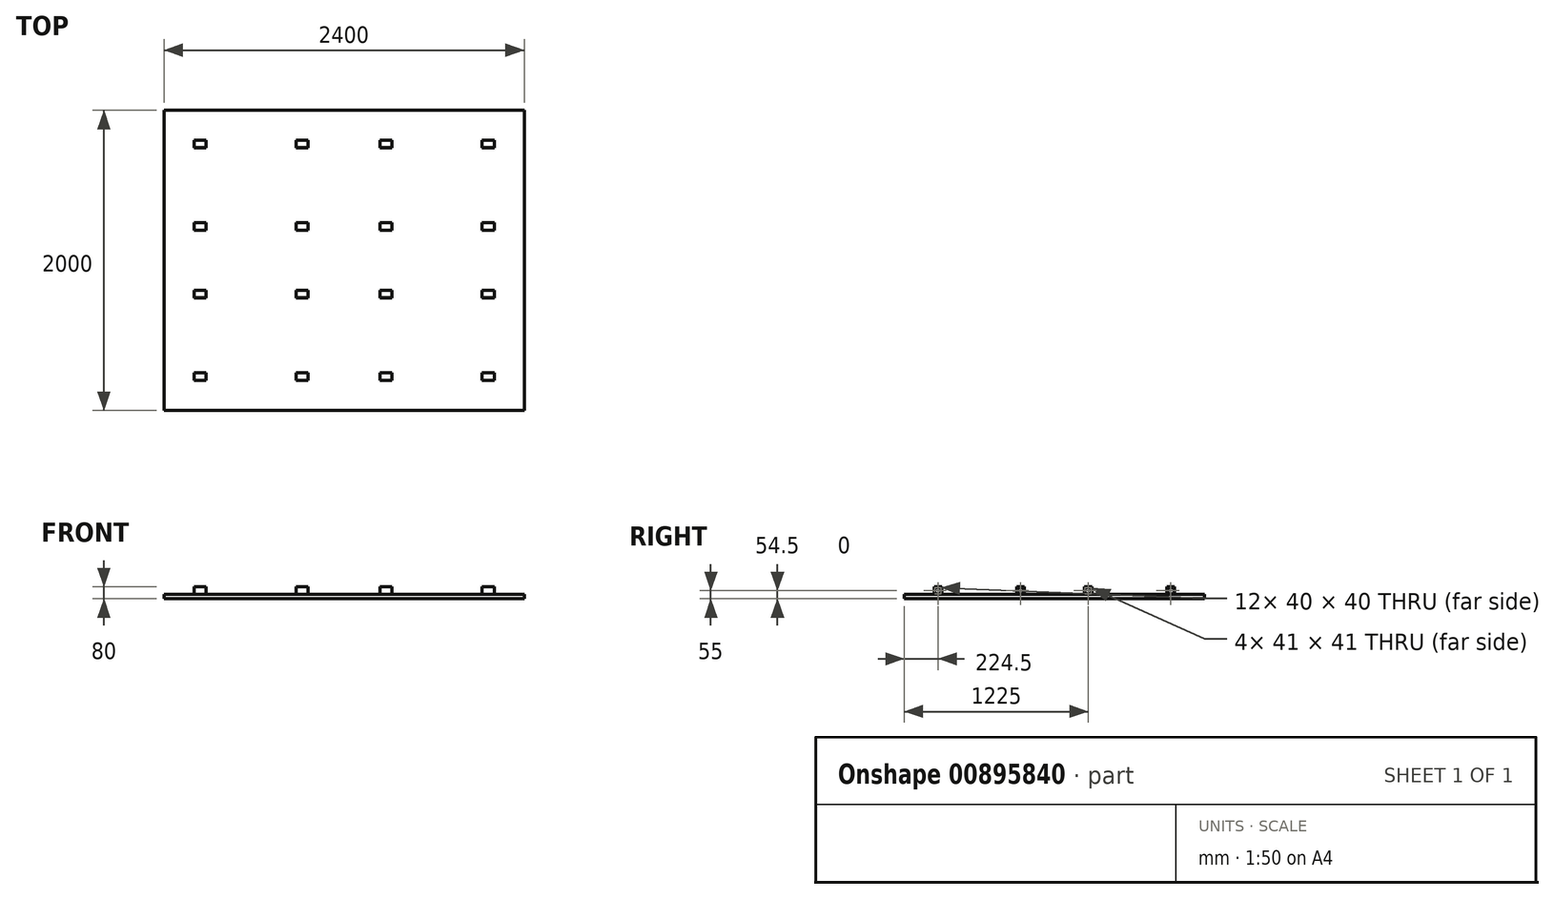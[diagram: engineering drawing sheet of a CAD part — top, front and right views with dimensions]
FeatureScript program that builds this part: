
annotation { "Feature Type Name" : "Feature", "Feature Type Description" : "" }
export const myFeature = defineFeature(function(context is Context, id is Id, definition is map)
    precondition{}
    {
        {
            var Q0;
            Q0=qCreatedBy(makeId("Top.planeOp"),FACE);
            var sketch = newSketch(context, id + "F0", { "sketchPlane" : qUnion([Q0])});
            skLineSegment(sketch, "E0.bottom", {"start": v(0, 0) * mm, "end": v(1200, 0) * mm});
            skLineSegment(sketch, "E0.top", {"start": v(0, 1000) * mm, "end": v(1200, 1000) * mm});
            skLineSegment(sketch, "E0.left", {"start": v(0, 0) * mm, "end": v(0, 1000) * mm});
            skLineSegment(sketch, "E0.right", {"start": v(1200, 0) * mm, "end": v(1200, 1000) * mm});
            skLineSegment(sketch, "E1.MirrorCS", {"start": v(1200, 0) * mm, "end": v(1200, -1000) * mm});
            skLineSegment(sketch, "E2.MirrorCS", {"start": v(0, -1000) * mm, "end": v(1200, -1000) * mm});
            skLineSegment(sketch, "E3.MirrorCS", {"start": v(0, 0) * mm, "end": v(0, -1000) * mm});
            skLineSegment(sketch, "E4.MirrorCS", {"start": v(0, 1000) * mm, "end": v(-1200, 1000) * mm});
            skLineSegment(sketch, "E5.MirrorCS", {"start": v(0, 0) * mm, "end": v(-1200, 0) * mm});
            skLineSegment(sketch, "E6.MirrorCS", {"start": v(-1200, 0) * mm, "end": v(-1200, 1000) * mm});
            skLineSegment(sketch, "E7.MirrorCS", {"start": v(0, -1000) * mm, "end": v(-1200, -1000) * mm});
            skLineSegment(sketch, "E8.MirrorCS", {"start": v(-1200, 0) * mm, "end": v(-1200, -1000) * mm});
            skSolve(sketch);
        }
        {
            var Q0;
            Q0=makeQuery(id+"F0.imprint","IMPRINT",FACE,{"disambiguationData":[TD([[makeQuery(id+"F0.imprint","IMPRINT",EDGE,{"derivedFrom":sQuery(id+"F0.wireOp",EDGE,"E4.MirrorCS")}),1.0]])]});
            var Q1;
            Q1=makeQuery(id+"F0.imprint","IMPRINT",FACE,{"disambiguationData":[TD([[makeQuery(id+"F0.imprint","IMPRINT",EDGE,{"derivedFrom":sQuery(id+"F0.wireOp",EDGE,"E0.top")}),-1.0]])]});
            var Q2;
            Q2=makeQuery(id+"F0.imprint","IMPRINT",FACE,{"disambiguationData":[TD([[makeQuery(id+"F0.imprint","IMPRINT",EDGE,{"derivedFrom":sQuery(id+"F0.wireOp",EDGE,"E1.MirrorCS")}),-1.0]])]});
            var Q3;
            Q3=makeQuery(id+"F0.imprint","IMPRINT",FACE,{"disambiguationData":[TD([[makeQuery(id+"F0.imprint","IMPRINT",EDGE,{"derivedFrom":sQuery(id+"F0.wireOp",EDGE,"E5.MirrorCS")}),1.0]])]});
            extrude(context, id + "F1", {"entities" : qUnion([Q0, Q1, Q2, Q3]), "depth" : 30 * mm, "offsetDistance" : 25 * mm});
        }
        {
            var Q0;
            Q0=makeQuery(id+"F1.opExtrude","CAP_FACE",FACE,{"disambiguationData":[OSD([sQuery(id+"F0.wireOp",EDGE,"E0.top"),sQuery(id+"F0.wireOp",EDGE,"E0.right"),sQuery(id+"F0.wireOp",EDGE,"E1.MirrorCS"),sQuery(id+"F0.wireOp",EDGE,"E2.MirrorCS"),sQuery(id+"F0.wireOp",EDGE,"E4.MirrorCS"),sQuery(id+"F0.wireOp",EDGE,"E6.MirrorCS"),sQuery(id+"F0.wireOp",EDGE,"E7.MirrorCS"),sQuery(id+"F0.wireOp",EDGE,"E8.MirrorCS")])],"isStart":false});
            var sketch = newSketch(context, id + "F2", { "sketchPlane" : qUnion([Q0])});
            skLineSegment(sketch, "E9.bottom", {"start": v(-1000, 800) * mm, "end": v(-920, 800) * mm});
            skLineSegment(sketch, "E9.top", {"start": v(-1000, 750) * mm, "end": v(-920, 750) * mm});
            skLineSegment(sketch, "E9.left", {"start": v(-1000, 800) * mm, "end": v(-1000, 750) * mm});
            skLineSegment(sketch, "E9.right", {"start": v(-920, 800) * mm, "end": v(-920, 750) * mm});
            skLineSegment(sketch, "E10.bottom", {"start": v(-320, 800) * mm, "end": v(-240, 800) * mm});
            skLineSegment(sketch, "E10.top", {"start": v(-320, 750) * mm, "end": v(-240, 750) * mm});
            skLineSegment(sketch, "E10.left", {"start": v(-320, 800) * mm, "end": v(-320, 750) * mm});
            skLineSegment(sketch, "E10.right", {"start": v(-240, 800) * mm, "end": v(-240, 750) * mm});
            skLineSegment(sketch, "E11.bottom", {"start": v(240, 800) * mm, "end": v(320, 800) * mm});
            skLineSegment(sketch, "E11.top", {"start": v(240, 750) * mm, "end": v(320, 750) * mm});
            skLineSegment(sketch, "E11.left", {"start": v(240, 800) * mm, "end": v(240, 750) * mm});
            skLineSegment(sketch, "E11.right", {"start": v(320, 800) * mm, "end": v(320, 750) * mm});
            skLineSegment(sketch, "E12.bottom", {"start": v(920, 800) * mm, "end": v(1000, 800) * mm});
            skLineSegment(sketch, "E12.top", {"start": v(920, 750) * mm, "end": v(1000, 750) * mm});
            skLineSegment(sketch, "E12.left", {"start": v(920, 800) * mm, "end": v(920, 750) * mm});
            skLineSegment(sketch, "E12.right", {"start": v(1000, 800) * mm, "end": v(1000, 750) * mm});
            skLineSegment(sketch, "E13.MirrorCS", {"start": v(-1000, -800) * mm, "end": v(-1000, -750) * mm});
            skLineSegment(sketch, "E14.MirrorCS", {"start": v(-1000, -800) * mm, "end": v(-920, -800) * mm});
            skLineSegment(sketch, "E15.MirrorCS", {"start": v(-920, -800) * mm, "end": v(-920, -750) * mm});
            skLineSegment(sketch, "E16.MirrorCS", {"start": v(-1000, -750) * mm, "end": v(-920, -750) * mm});
            skLineSegment(sketch, "E17.MirrorCS", {"start": v(-320, -800) * mm, "end": v(-240, -800) * mm});
            skLineSegment(sketch, "E18.MirrorCS", {"start": v(-240, -800) * mm, "end": v(-240, -750) * mm});
            skLineSegment(sketch, "E19.MirrorCS", {"start": v(-320, -750) * mm, "end": v(-240, -750) * mm});
            skLineSegment(sketch, "E20.MirrorCS", {"start": v(-320, -800) * mm, "end": v(-320, -750) * mm});
            skLineSegment(sketch, "E21.MirrorCS", {"start": v(240, -800) * mm, "end": v(320, -800) * mm});
            skLineSegment(sketch, "E22.MirrorCS", {"start": v(240, -800) * mm, "end": v(240, -750) * mm});
            skLineSegment(sketch, "E23.MirrorCS", {"start": v(240, -750) * mm, "end": v(320, -750) * mm});
            skLineSegment(sketch, "E24.MirrorCS", {"start": v(320, -800) * mm, "end": v(320, -750) * mm});
            skLineSegment(sketch, "E25.MirrorCS", {"start": v(920, -800) * mm, "end": v(1000, -800) * mm});
            skLineSegment(sketch, "E26.MirrorCS", {"start": v(920, -800) * mm, "end": v(920, -750) * mm});
            skLineSegment(sketch, "E27.MirrorCS", {"start": v(920, -750) * mm, "end": v(1000, -750) * mm});
            skLineSegment(sketch, "E28.MirrorCS", {"start": v(1000, -800) * mm, "end": v(1000, -750) * mm});
            skLineSegment(sketch, "E29.bottom", {"start": v(-1000, 250) * mm, "end": v(-920, 250) * mm});
            skLineSegment(sketch, "E29.top", {"start": v(-1000, 200) * mm, "end": v(-920, 200) * mm});
            skLineSegment(sketch, "E29.left", {"start": v(-1000, 250) * mm, "end": v(-1000, 200) * mm});
            skLineSegment(sketch, "E29.right", {"start": v(-920, 250) * mm, "end": v(-920, 200) * mm});
            skLineSegment(sketch, "E30.bottom", {"start": v(-320, 250) * mm, "end": v(-240, 250) * mm});
            skLineSegment(sketch, "E30.top", {"start": v(-320, 200) * mm, "end": v(-240, 200) * mm});
            skLineSegment(sketch, "E30.left", {"start": v(-320, 250) * mm, "end": v(-320, 200) * mm});
            skLineSegment(sketch, "E30.right", {"start": v(-240, 250) * mm, "end": v(-240, 200) * mm});
            skLineSegment(sketch, "E31.bottom", {"start": v(240, 250) * mm, "end": v(320, 250) * mm});
            skLineSegment(sketch, "E31.top", {"start": v(240, 200) * mm, "end": v(320, 200) * mm});
            skLineSegment(sketch, "E31.left", {"start": v(240, 250) * mm, "end": v(240, 200) * mm});
            skLineSegment(sketch, "E31.right", {"start": v(320, 250) * mm, "end": v(320, 200) * mm});
            skLineSegment(sketch, "E32.bottom", {"start": v(920, 250) * mm, "end": v(1000, 250) * mm});
            skLineSegment(sketch, "E32.top", {"start": v(920, 200) * mm, "end": v(1000, 200) * mm});
            skLineSegment(sketch, "E32.left", {"start": v(920, 250) * mm, "end": v(920, 200) * mm});
            skLineSegment(sketch, "E32.right", {"start": v(1000, 250) * mm, "end": v(1000, 200) * mm});
            skLineSegment(sketch, "E33.MirrorCS", {"start": v(-1000, -250) * mm, "end": v(-920, -250) * mm});
            skLineSegment(sketch, "E34.MirrorCS", {"start": v(-920, -250) * mm, "end": v(-920, -200) * mm});
            skLineSegment(sketch, "E35.MirrorCS", {"start": v(-1000, -200) * mm, "end": v(-920, -200) * mm});
            skLineSegment(sketch, "E36.MirrorCS", {"start": v(-1000, -250) * mm, "end": v(-1000, -200) * mm});
            skLineSegment(sketch, "E37.MirrorCS", {"start": v(-320, -250) * mm, "end": v(-320, -200) * mm});
            skLineSegment(sketch, "E38.MirrorCS", {"start": v(-320, -250) * mm, "end": v(-240, -250) * mm});
            skLineSegment(sketch, "E39.MirrorCS", {"start": v(-240, -250) * mm, "end": v(-240, -200) * mm});
            skLineSegment(sketch, "E40.MirrorCS", {"start": v(-320, -200) * mm, "end": v(-240, -200) * mm});
            skLineSegment(sketch, "E41.MirrorCS", {"start": v(240, -250) * mm, "end": v(320, -250) * mm});
            skLineSegment(sketch, "E42.MirrorCS", {"start": v(320, -250) * mm, "end": v(320, -200) * mm});
            skLineSegment(sketch, "E43.MirrorCS", {"start": v(240, -200) * mm, "end": v(320, -200) * mm});
            skLineSegment(sketch, "E44.MirrorCS", {"start": v(240, -250) * mm, "end": v(240, -200) * mm});
            skLineSegment(sketch, "E45.MirrorCS", {"start": v(920, -250) * mm, "end": v(1000, -250) * mm});
            skLineSegment(sketch, "E46.MirrorCS", {"start": v(1000, -250) * mm, "end": v(1000, -200) * mm});
            skLineSegment(sketch, "E47.MirrorCS", {"start": v(920, -200) * mm, "end": v(1000, -200) * mm});
            skLineSegment(sketch, "E48.MirrorCS", {"start": v(920, -250) * mm, "end": v(920, -200) * mm});
            skSolve(sketch);
        }
        {
            var Q0;
            Q0 = qSketchRegion(id + "F2", true);
            extrude(context, id + "F3", {"entities" : qUnion([Q0]), "operationType" : NewBodyOperationType.ADD, "depth" : 50 * mm, "offsetDistance" : 25 * mm});
        }
        {
            var Q0;
            Q0=makeQuery(id+"F3.opExtrude","SWEPT_FACE",FACE,{"disambiguationData":[OSD([sQuery(id+"F2.wireOp",EDGE,"E29.left")])]});
            var sketch = newSketch(context, id + "F4", { "sketchPlane" : qUnion([Q0])});
            skLineSegment(sketch, "E49.bottom", {"start": v(-245.5, 75.5) * mm, "end": v(-204.5, 75.5) * mm});
            skLineSegment(sketch, "E49.top", {"start": v(-245.5, 34.5) * mm, "end": v(-204.5, 34.5) * mm});
            skLineSegment(sketch, "E49.left", {"start": v(-245.5, 75.5) * mm, "end": v(-245.5, 34.5) * mm});
            skLineSegment(sketch, "E49.right", {"start": v(-204.5, 75.5) * mm, "end": v(-204.5, 34.5) * mm});
            skLineSegment(sketch, "E50.bottom", {"start": v(-795.5, 74.5) * mm, "end": v(-755.5, 74.5) * mm});
            skLineSegment(sketch, "E50.top", {"start": v(-795.5, 34.5) * mm, "end": v(-755.5, 34.5) * mm});
            skLineSegment(sketch, "E50.left", {"start": v(-795.5, 74.5) * mm, "end": v(-795.5, 34.5) * mm});
            skLineSegment(sketch, "E50.right", {"start": v(-755.5, 74.5) * mm, "end": v(-755.5, 34.5) * mm});
            skLineSegment(sketch, "E51.bottom", {"start": v(205.5, 74.5) * mm, "end": v(245.5, 74.5) * mm});
            skLineSegment(sketch, "E51.top", {"start": v(205.5, 34.5) * mm, "end": v(245.5, 34.5) * mm});
            skLineSegment(sketch, "E51.left", {"start": v(205.5, 74.5) * mm, "end": v(205.5, 34.5) * mm});
            skLineSegment(sketch, "E51.right", {"start": v(245.5, 74.5) * mm, "end": v(245.5, 34.5) * mm});
            skLineSegment(sketch, "E52.bottom", {"start": v(755.5, 74.5) * mm, "end": v(795.5, 74.5) * mm});
            skLineSegment(sketch, "E52.top", {"start": v(755.5, 34.5) * mm, "end": v(795.5, 34.5) * mm});
            skLineSegment(sketch, "E52.left", {"start": v(755.5, 74.5) * mm, "end": v(755.5, 34.5) * mm});
            skLineSegment(sketch, "E52.right", {"start": v(795.5, 74.5) * mm, "end": v(795.5, 34.5) * mm});
            skSolve(sketch);
        }
        {
            var Q0;
            Q0 = qSketchRegion(id + "F4", true);
            extrude(context, id + "F5", {"entities" : qUnion([Q0]), "operationType" : NewBodyOperationType.REMOVE, "oppositeDirection" : true, "depth" : 2200 * mm, "offsetDistance" : 25 * mm});
        }
    });
